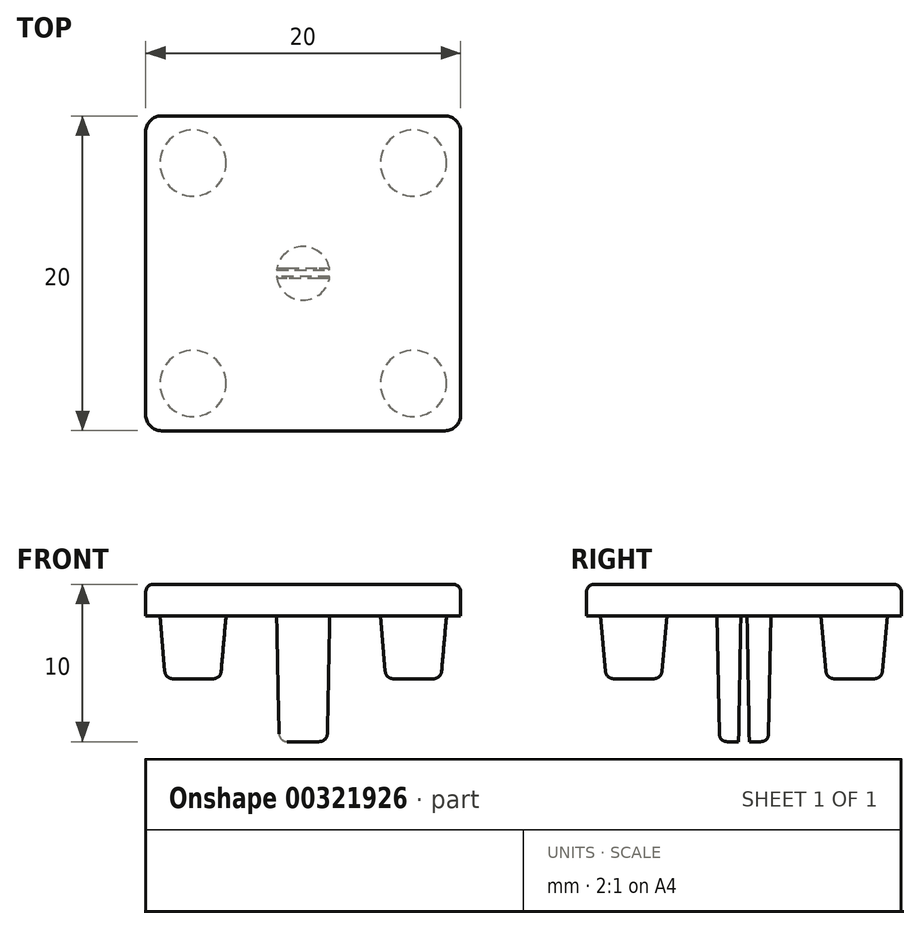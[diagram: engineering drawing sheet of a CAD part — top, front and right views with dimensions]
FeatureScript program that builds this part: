
annotation { "Feature Type Name" : "Feature", "Feature Type Description" : "" }
export const myFeature = defineFeature(function(context is Context, id is Id, definition is map)
    precondition{}
    {
        {
            var Q0;
            Q0=qCreatedBy(makeId("Top.planeOp"),FACE);
            var sketch = newSketch(context, id + "F0", { "sketchPlane" : qUnion([Q0])});
            skLineSegment(sketch, "E0.bottom", {"start": v(-59.56, 49.73) * mm, "end": v(-39.56, 49.73) * mm});
            skLineSegment(sketch, "E0.top", {"start": v(-59.56, 29.73) * mm, "end": v(-39.56, 29.73) * mm});
            skLineSegment(sketch, "E0.left", {"start": v(-59.56, 49.73) * mm, "end": v(-59.56, 29.73) * mm});
            skLineSegment(sketch, "E0.right", {"start": v(-39.56, 49.73) * mm, "end": v(-39.56, 29.73) * mm});
            skCircle(sketch, "E1", {"center": v(-49.56, 39.73) * mm, "radius": 1.7 * mm});
            skPoint(sketch, "E1.centerSnap0", {"position": v(-59.56, 39.73) * mm});
            skPoint(sketch, "E1.centerSnap1", {"position": v(-49.56, 49.73) * mm});
            skCircle(sketch, "E2", {"center": v(-56.56, 46.73) * mm, "radius": 2.1 * mm});
            skCircle(sketch, "E3", {"center": v(-42.56, 46.73) * mm, "radius": 2.1 * mm});
            skCircle(sketch, "E4", {"center": v(-42.56, 32.73) * mm, "radius": 2.1 * mm});
            skCircle(sketch, "E5", {"center": v(-56.56, 32.73) * mm, "radius": 2.1 * mm});
            skLineSegment(sketch, "E6", {"start": v(-47.87, 39.93) * mm, "end": v(-51.25, 39.93) * mm});
            skLineSegment(sketch, "E7", {"start": v(-47.87, 39.53) * mm, "end": v(-51.25, 39.53) * mm});
            skSolve(sketch);
        }
        {
            var Q0;
            Q0=makeQuery(id+"F0.imprint","IMPRINT",FACE,{"disambiguationData":[TD([[makeQuery(id+"F0.imprint","IMPRINT",EDGE,{"derivedFrom":sQuery(id+"F0.wireOp",EDGE,"E0.bottom")}),-1.0]])]});
            var Q1;
            Q1=makeQuery(id+"F0.imprint","IMPRINT",FACE,{"disambiguationData":[TD([[makeQuery(id+"F0.imprint","IMPRINT",EDGE,{"derivedFrom":sQuery(id+"F0.wireOp",EDGE,"E3")}),1.0]])]});
            var Q2;
            Q2=makeQuery(id+"F0.imprint","IMPRINT",FACE,{"disambiguationData":[TD([[makeQuery(id+"F0.imprint","IMPRINT",EDGE,{"derivedFrom":sQuery(id+"F0.wireOp",EDGE,"E4")}),1.0]])]});
            var Q3;
            Q3=makeQuery(id+"F0.imprint","IMPRINT",FACE,{"disambiguationData":[TD([[makeQuery(id+"F0.imprint","IMPRINT",EDGE,{"derivedFrom":sQuery(id+"F0.wireOp",EDGE,"E5")}),1.0]])]});
            var Q4;
            Q4=makeQuery(id+"F0.imprint","IMPRINT",FACE,{"disambiguationData":[TD([[makeQuery(id+"F0.imprint","IMPRINT",EDGE,{"derivedFrom":sQuery(id+"F0.wireOp",EDGE,"E2")}),1.0]])]});
            var Q5;
            Q5=makeQuery(id+"F0.imprint","IMPRINT",FACE,{"disambiguationData":[TD([[makeQuery(id+"F0.imprint","IMPRINT",EDGE,{"derivedFrom":sQuery(id+"F0.wireOp",EDGE,"E1")}),1.0]])]});
            var Q6;
            {var subQ0=sQuery(id+"F0.wireOp",EDGE,"E6");Q6=makeQuery(id+"F0.imprint","IMPRINT",FACE,{"disambiguationData":[TD([[makeQuery(id+"F0.imprint","IMPRINT",EDGE,{"derivedFrom":subQ0}),-1.0]])]});}
            var Q7;
            {var subQ0=sQuery(id+"F0.wireOp",EDGE,"E7");Q7=makeQuery(id+"F0.imprint","IMPRINT",FACE,{"disambiguationData":[TD([[makeQuery(id+"F0.imprint","IMPRINT",EDGE,{"derivedFrom":subQ0}),1.0]])]});}
            extrude(context, id + "F1", {"entities" : qUnion([Q0, Q1, Q2, Q3, Q4, Q5, Q6, Q7]), "depth" : 2 * mm});
        }
        {
            var Q0;
            Q0=makeQuery(id+"F0.imprint","IMPRINT",FACE,{"disambiguationData":[TD([[makeQuery(id+"F0.imprint","IMPRINT",EDGE,{"derivedFrom":sQuery(id+"F0.wireOp",EDGE,"E3")}),1.0]])]});
            var Q1;
            Q1=makeQuery(id+"F0.imprint","IMPRINT",FACE,{"disambiguationData":[TD([[makeQuery(id+"F0.imprint","IMPRINT",EDGE,{"derivedFrom":sQuery(id+"F0.wireOp",EDGE,"E2")}),1.0]])]});
            var Q2;
            Q2=makeQuery(id+"F0.imprint","IMPRINT",FACE,{"disambiguationData":[TD([[makeQuery(id+"F0.imprint","IMPRINT",EDGE,{"derivedFrom":sQuery(id+"F0.wireOp",EDGE,"E5")}),1.0]])]});
            var Q3;
            Q3=makeQuery(id+"F0.imprint","IMPRINT",FACE,{"disambiguationData":[TD([[makeQuery(id+"F0.imprint","IMPRINT",EDGE,{"derivedFrom":sQuery(id+"F0.wireOp",EDGE,"E4")}),1.0]])]});
            extrude(context, id + "F2", {"entities" : qUnion([Q0, Q1, Q2, Q3]), "operationType" : NewBodyOperationType.ADD, "oppositeDirection" : true, "depth" : 4 * mm, "hasDraft" : true, "draftAngle" : 5 * degree, "draftPullDirection" : true});
        }
        {
            var Q0;
            {var subQ0=sQuery(id+"F0.wireOp",EDGE,"E6");Q0=makeQuery(id+"F0.imprint","IMPRINT",FACE,{"disambiguationData":[TD([[makeQuery(id+"F0.imprint","IMPRINT",EDGE,{"derivedFrom":subQ0}),-1.0]])]});}
            var Q1;
            {var subQ0=sQuery(id+"F0.wireOp",EDGE,"E7");Q1=makeQuery(id+"F0.imprint","IMPRINT",FACE,{"disambiguationData":[TD([[makeQuery(id+"F0.imprint","IMPRINT",EDGE,{"derivedFrom":subQ0}),1.0]])]});}
            extrude(context, id + "F3", {"entities" : qUnion([Q0, Q1]), "operationType" : NewBodyOperationType.ADD, "oppositeDirection" : true, "depth" : 8 * mm, "hasDraft" : true, "draftAngle" : 1 * degree, "draftPullDirection" : true});
        }
        {
            var Q0;
            Q0=makeQuery(id+"F1.opExtrude","SWEPT_EDGE",EDGE,{"disambiguationData":[OSD([sQuery(id+"F0.wireOp",EDGE,"E0.bottom"),sQuery(id+"F0.wireOp",EDGE,"E0.right")])]});
            var Q1;
            Q1=makeQuery(id+"F1.opExtrude","SWEPT_EDGE",EDGE,{"disambiguationData":[OSD([sQuery(id+"F0.wireOp",EDGE,"E0.top"),sQuery(id+"F0.wireOp",EDGE,"E0.right")])]});
            var Q2;
            Q2=makeQuery(id+"F1.opExtrude","SWEPT_EDGE",EDGE,{"disambiguationData":[OSD([sQuery(id+"F0.wireOp",EDGE,"E0.bottom"),sQuery(id+"F0.wireOp",EDGE,"E0.left")])]});
            var Q3;
            Q3=makeQuery(id+"F1.opExtrude","SWEPT_EDGE",EDGE,{"disambiguationData":[OSD([sQuery(id+"F0.wireOp",EDGE,"E0.top"),sQuery(id+"F0.wireOp",EDGE,"E0.left")])]});
            fillet(context, id + "F4", {"entities" : qUnion([Q0, Q1, Q2, Q3]), "radius" : 1 * mm, "tangentPropagation" : true, "allowEdgeOverflow" : false});
        }
        {
            var Q0;
            Q0=makeQuery(id+"F1.opExtrude","CAP_FACE",FACE,{"disambiguationData":[OSD([sQuery(id+"F0.wireOp",EDGE,"E0.bottom"),sQuery(id+"F0.wireOp",EDGE,"E0.top"),sQuery(id+"F0.wireOp",EDGE,"E0.left"),sQuery(id+"F0.wireOp",EDGE,"E0.right")])],"isStart":false});
            var Q1;
            Q1=makeQuery(id+"F2.opExtrude","CAP_FACE",FACE,{"disambiguationData":[OSD([sQuery(id+"F0.wireOp",EDGE,"E3")])],"isStart":false});
            var Q2;
            Q2=makeQuery(id+"F2.opExtrude","CAP_FACE",FACE,{"disambiguationData":[OSD([sQuery(id+"F0.wireOp",EDGE,"E2")])],"isStart":false});
            var Q3;
            Q3=makeQuery(id+"F2.opExtrude","CAP_FACE",FACE,{"disambiguationData":[OSD([sQuery(id+"F0.wireOp",EDGE,"E5")])],"isStart":false});
            var Q4;
            Q4=makeQuery(id+"F2.opExtrude","CAP_FACE",FACE,{"disambiguationData":[OSD([sQuery(id+"F0.wireOp",EDGE,"E4")])],"isStart":false});
            var Q5;
            {var subQ0=sQuery(id+"F0.wireOp",EDGE,"E7");var subQ1=sQuery(id+"F0.wireOp",EDGE,"E1");Q5=makeQuery(id+"F3.opExtrude","CAP_EDGE",EDGE,{"disambiguationData":[OSD([subQ1]),TDD([makeQuery(id+"F0.imprint","IMPRINT",EDGE,{"disambiguationData":[TD([[makeQuery(id+"F0.imprint","INTERSECT",VERTEX,{"disambiguationData":[OD(0.0)],"derivedFrom":[subQ1,subQ0]}),1.0]])],"derivedFrom":subQ1})])],"isStart":false});}
            var Q6;
            {var subQ0=sQuery(id+"F0.wireOp",EDGE,"E6");var subQ1=sQuery(id+"F0.wireOp",EDGE,"E1");Q6=makeQuery(id+"F3.opExtrude","CAP_EDGE",EDGE,{"disambiguationData":[OSD([subQ1]),TDD([makeQuery(id+"F0.imprint","IMPRINT",EDGE,{"disambiguationData":[TD([[makeQuery(id+"F0.imprint","INTERSECT",VERTEX,{"disambiguationData":[OD(0.0)],"derivedFrom":[subQ1,subQ0]}),-1.0]])],"derivedFrom":subQ1})])],"isStart":false});}
            var Q7;
            Q7=makeQuery(id+"F2.opExtrude","CAP_EDGE",EDGE,{"disambiguationData":[OSD([sQuery(id+"F0.wireOp",EDGE,"E3")])],"isStart":true});
            var Q8;
            Q8=makeQuery(id+"F2.opExtrude","CAP_EDGE",EDGE,{"disambiguationData":[OSD([sQuery(id+"F0.wireOp",EDGE,"E4")])],"isStart":true});
            var Q9;
            Q9=makeQuery(id+"F2.opExtrude","CAP_EDGE",EDGE,{"disambiguationData":[OSD([sQuery(id+"F0.wireOp",EDGE,"E5")])],"isStart":true});
            var Q10;
            Q10=makeQuery(id+"F2.opExtrude","CAP_EDGE",EDGE,{"disambiguationData":[OSD([sQuery(id+"F0.wireOp",EDGE,"E2")])],"isStart":true});
            var Q11;
            {var subQ0=sQuery(id+"F0.wireOp",EDGE,"E7");var subQ1=sQuery(id+"F0.wireOp",EDGE,"E1");Q11=makeQuery(id+"F3.opExtrude","CAP_EDGE",EDGE,{"disambiguationData":[OSD([subQ1]),TDD([makeQuery(id+"F0.imprint","IMPRINT",EDGE,{"disambiguationData":[TD([[makeQuery(id+"F0.imprint","INTERSECT",VERTEX,{"disambiguationData":[OD(0.0)],"derivedFrom":[subQ1,subQ0]}),1.0]])],"derivedFrom":subQ1})])],"isStart":true});}
            var Q12;
            {var subQ0=sQuery(id+"F0.wireOp",EDGE,"E6");var subQ1=sQuery(id+"F0.wireOp",EDGE,"E1");Q12=makeQuery(id+"F3.opExtrude","CAP_EDGE",EDGE,{"disambiguationData":[OSD([subQ1]),TDD([makeQuery(id+"F0.imprint","IMPRINT",EDGE,{"disambiguationData":[TD([[makeQuery(id+"F0.imprint","INTERSECT",VERTEX,{"disambiguationData":[OD(0.0)],"derivedFrom":[subQ1,subQ0]}),-1.0]])],"derivedFrom":subQ1})])],"isStart":true});}
            fillet(context, id + "F5", {"entities" : qUnion([Q0, Q1, Q2, Q3, Q4, Q5, Q6, Q7, Q8, Q9, Q10, Q11, Q12]), "radius" : 0.5 * mm, "tangentPropagation" : true, "allowEdgeOverflow" : false});
        }
    });
